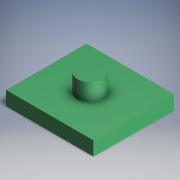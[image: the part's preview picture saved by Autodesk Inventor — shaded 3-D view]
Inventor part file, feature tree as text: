
AUTODESK INVENTOR PART (.ipt)
format: ipt  version: 2018 (Build 220112000, 112)  size: 121,856 bytes
history: native  units: in
note: dims shown in document units (in); Inventor stores cm internally (conversion verified against a paired STEP export)
features: extrude x2, sketch x2
ambient origin geometry x8: Origin, YZ Plane, XZ Plane, XY Plane, X Axis, Y Axis, Z Axis, Center Point
bodies: Solid1 (feature_tree)
feature tree (4):
  extrude  "Extrusion1"  Depth=0.9055in
  extrude  "Extrusion2"  Depth=0.1969in
  sketch  "Sketch1"  dims[d0=0.9843in d1=0.9055in]
  sketch  "Sketch2"  dims[d2=0.1575in d3=0.0in d4=0.2846in d5=0.4921in d6=0.4528in d7=0.1969in d8=0.0in]
